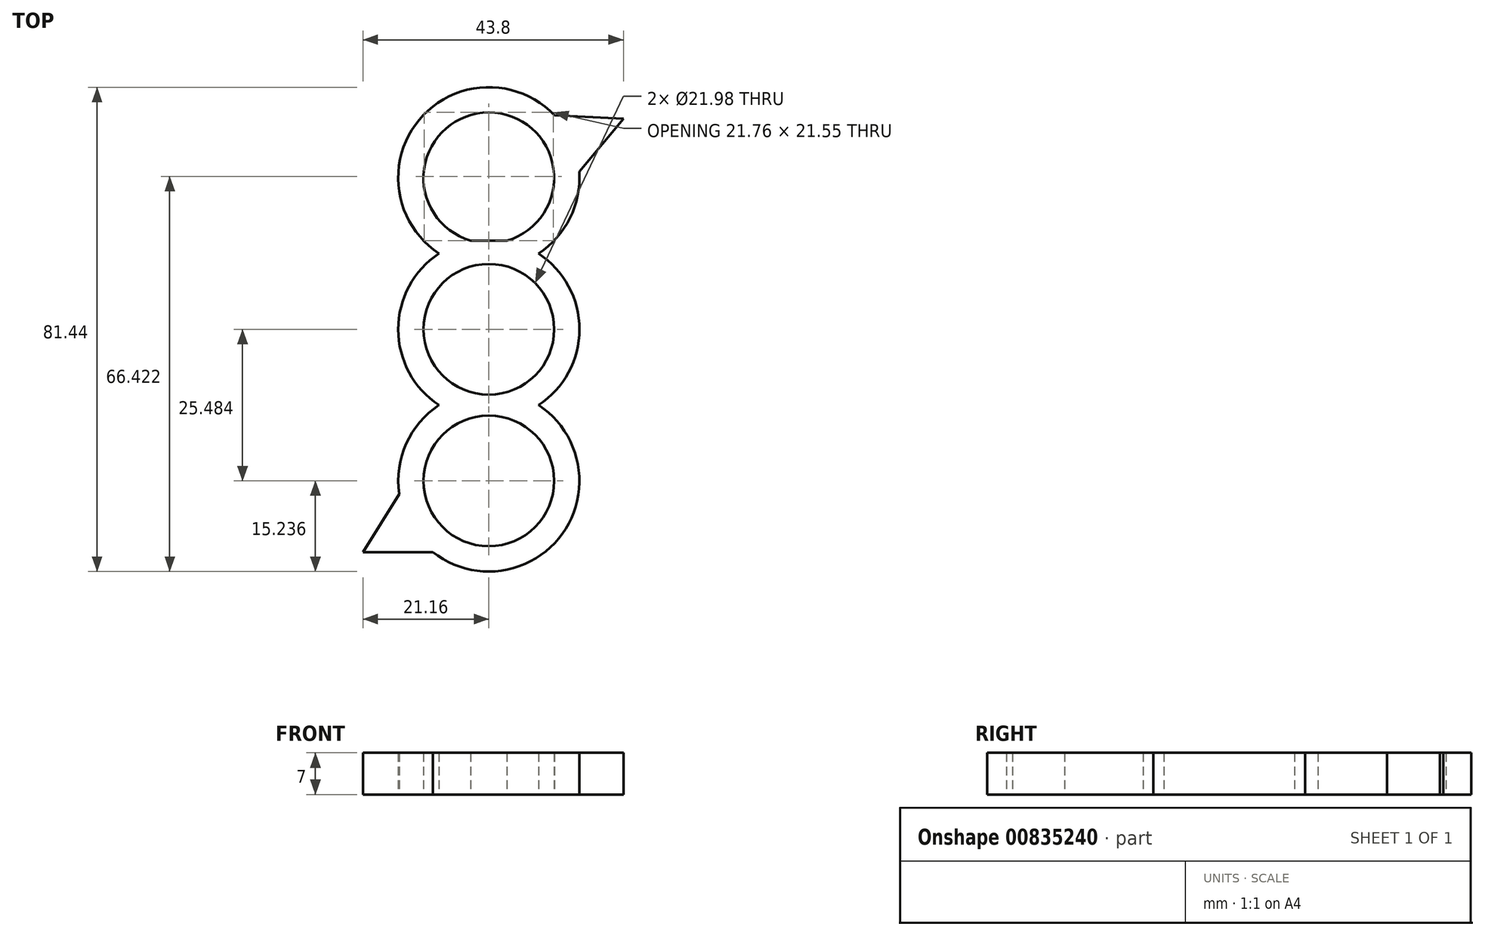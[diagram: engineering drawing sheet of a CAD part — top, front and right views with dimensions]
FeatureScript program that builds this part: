
annotation { "Feature Type Name" : "Feature", "Feature Type Description" : "" }
export const myFeature = defineFeature(function(context is Context, id is Id, definition is map)
    precondition{}
    {
        {
            var Q0;
            Q0=qCreatedBy(makeId("Top.planeOp"),FACE);
            var sketch = newSketch(context, id + "F0", { "sketchPlane" : qUnion([Q0])});
            skCircle(sketch, "E0", {"center": v(0, 0) * mm, "radius": 11 * mm});
            skArc(sketch, "E1", {"start": v(0, 14.5) * mm, "mid": v(1.55, 36.37) * mm, "end": v(-3.07, 14.93) * mm});
            skCircle(sketch, "E2", {"center": v(0, -25.48) * mm, "radius": 11 * mm});
            skLineSegment(sketch, "E3", {"start": v(0, 25.48) * mm, "end": v(0, -25.48) * mm, "construction": true});
            skLineSegment(sketch, "E4.bottom", {"start": v(-29.85, 57.15) * mm, "end": v(29.85, 57.15) * mm, "construction": true});
            skLineSegment(sketch, "E4.top", {"start": v(-29.85, -57.15) * mm, "end": v(29.85, -57.15) * mm, "construction": true});
            skLineSegment(sketch, "E4.left", {"start": v(-29.84, 57.15) * mm, "end": v(-29.85, -57.15) * mm, "construction": true});
            skLineSegment(sketch, "E4.right", {"start": v(29.85, 57.15) * mm, "end": v(29.84, -57.15) * mm, "construction": true});
            skPoint(sketch, "E5", {"position": v(0, 57.15) * mm});
            skPoint(sketch, "E6", {"position": v(-29.85, 0) * mm});
            skArc(sketch, "E7", {"start": v(8.36, 12.74) * mm, "mid": v(13.65, 18.71) * mm, "end": v(15.2, 26.54) * mm});
            skArc(sketch, "E8", {"start": v(-8.36, 12.74) * mm, "mid": v(-15.24, 0) * mm, "end": v(-8.36, -12.74) * mm});
            skArc(sketch, "E9", {"start": v(3.07, -10.56) * mm, "mid": v(0, -10.24) * mm, "end": v(-3.07, -10.56) * mm});
            skLineSegment(sketch, "E10", {"start": v(11.05, 35.98) * mm, "end": v(22.64, 35.44) * mm});
            skLineSegment(sketch, "E11", {"start": v(22.64, 35.44) * mm, "end": v(15.2, 26.54) * mm});
            skLineSegment(sketch, "E12", {"start": v(-15.08, -27.67) * mm, "end": v(-21.16, -37.46) * mm});
            skLineSegment(sketch, "E13", {"start": v(-21.16, -37.46) * mm, "end": v(-9.42, -37.46) * mm});
            skArc(sketch, "E14.trimOffspring", {"start": v(-3.07, 10.56) * mm, "mid": v(0, 10.24) * mm, "end": v(3.07, 10.56) * mm});
            skArc(sketch, "E15.trimOffspring", {"start": v(-8.36, -12.74) * mm, "mid": v(-13.9, -19.23) * mm, "end": v(-15.08, -27.67) * mm});
            skArc(sketch, "E16.trimOffspring", {"start": v(-3.07, -14.93) * mm, "mid": v(0, -15.24) * mm, "end": v(3.07, -14.93) * mm});
            skArc(sketch, "E17.trimOffspring", {"start": v(8.36, -12.74) * mm, "mid": v(15.24, 0) * mm, "end": v(8.36, 12.74) * mm});
            skArc(sketch, "E18.trimOffspring", {"start": v(-9.42, -37.46) * mm, "mid": v(12.37, -34.38) * mm, "end": v(8.36, -12.74) * mm});
            skArc(sketch, "E19.trimOffspring", {"start": v(11.05, 35.98) * mm, "mid": v(-11.7, 35.25) * mm, "end": v(-8.36, 12.74) * mm});
            skLineSegment(sketch, "E20", {"start": v(-3.07, 14.93) * mm, "end": v(3.07, 14.93) * mm});
            skSolve(sketch);
        }
        {
            var Q0;
            Q0 = qSketchRegion(id + "F0", true);
            extrude(context, id + "F1", {"entities" : qUnion([Q0]), "depth" : 7 * mm, "offsetDistance" : 25.4 * mm});
        }
    });
